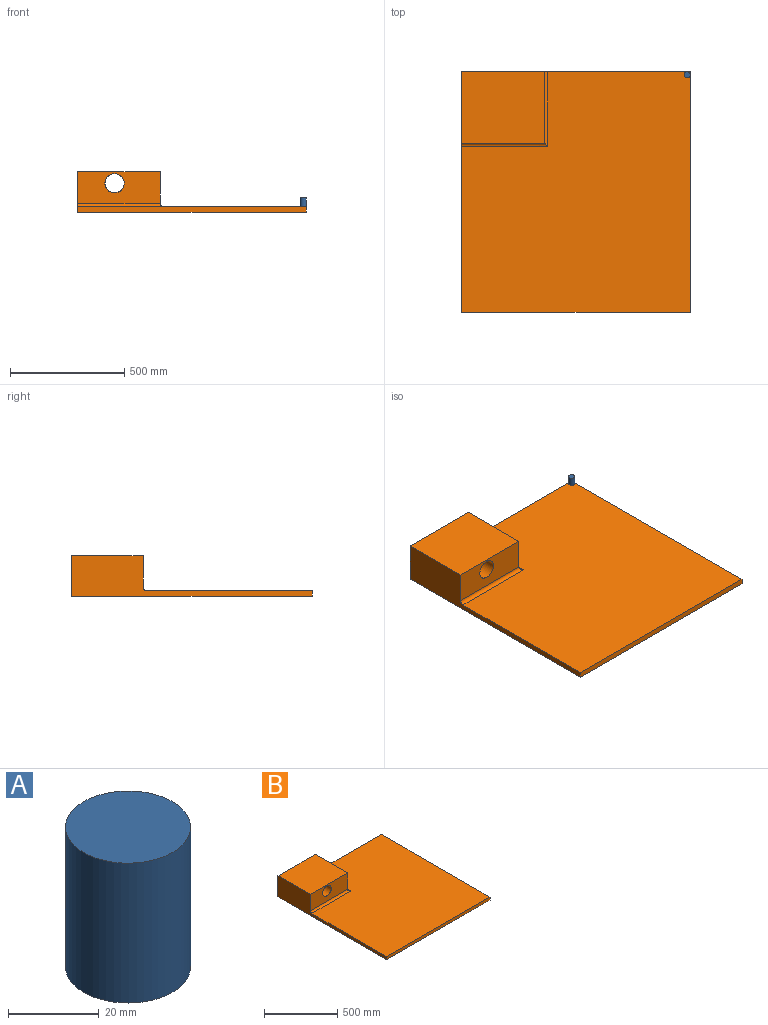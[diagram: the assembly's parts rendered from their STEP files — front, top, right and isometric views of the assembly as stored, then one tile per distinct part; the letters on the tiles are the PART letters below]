
ASSEMBLY  parts=2 mates=1
PART A: 3 faces, bbox 27.5x27.5x37.7 mm
  f0: cylinder r=13.77mm len=37.7mm, axis (0,0,-1), area 3262.3mm2, adj f1,f2
  f1: plane 27.54x27.54mm, normal (0,0,1), area 595.9mm2, adj f0
  f2: plane 27.54x27.54mm, normal (0,0,-1), area 595.9mm2, adj f0
PART B: 12 faces, bbox 1000x1052.4x177 mm
  f0: plane 1052.38x1000mm, normal (0,0,1), area 929190.5mm2, adj f1,f2,f3,f4,f9,f10
  f1: plane 1000x177mm, normal (0,1,0), area 74450.5mm2, adj f0,f2,f4,f5,f7,f8,f10,f11
  f2: plane 1052.38x177mm, normal (-1,0,0), area 73826.2mm2, adj f0,f1,f3,f5,f6,f8,f9
  f3: plane 1000x25mm, normal (0,-1,0), area 25000mm2, adj f0,f2,f4,f5
  f4: plane 1052.38x25mm, normal (1,0,0), area 26309.5mm2, adj f0,f1,f3,f5
  f5: plane 1052.38x1000mm, normal (0,0,-1), area 1052380.8mm2, adj f1,f2,f3,f4
  f6: plane 361.39x137mm, normal (0,-1,0), area 43981.3mm2, adj f2,f7,f8,f9,f11
  f7: plane 312.29x137mm, normal (1,0,0), area 42784.1mm2, adj f1,f6,f8,f10
  f8: plane 361.39x312.29mm, normal (0,0,1), area 112860mm2, adj f1,f2,f6,f7
  f9: cylinder r=15mm len=376.39mm, axis (1,0,0), area 8643.5mm2, adj f0,f2,f6,f10
  f10: cylinder r=15mm len=327.29mm, axis (0,1,0), area 7486.6mm2, adj f0,f1,f7,f9
  f11: cylinder r=41.95mm len=312.29mm, axis (0,-1,0), area 82320.2mm2, adj f1,f6
PLACE A rot(axis=(0,0,-1),48.6deg) t=(67.89,473.53,241.67)mm
PLACE B t=(-378.59,-74.14,216.67)mm fixed
MATE planar A.f0 <-> B.f0  axis (0,0,-1) through (67.89,473.53,241.67)mm
